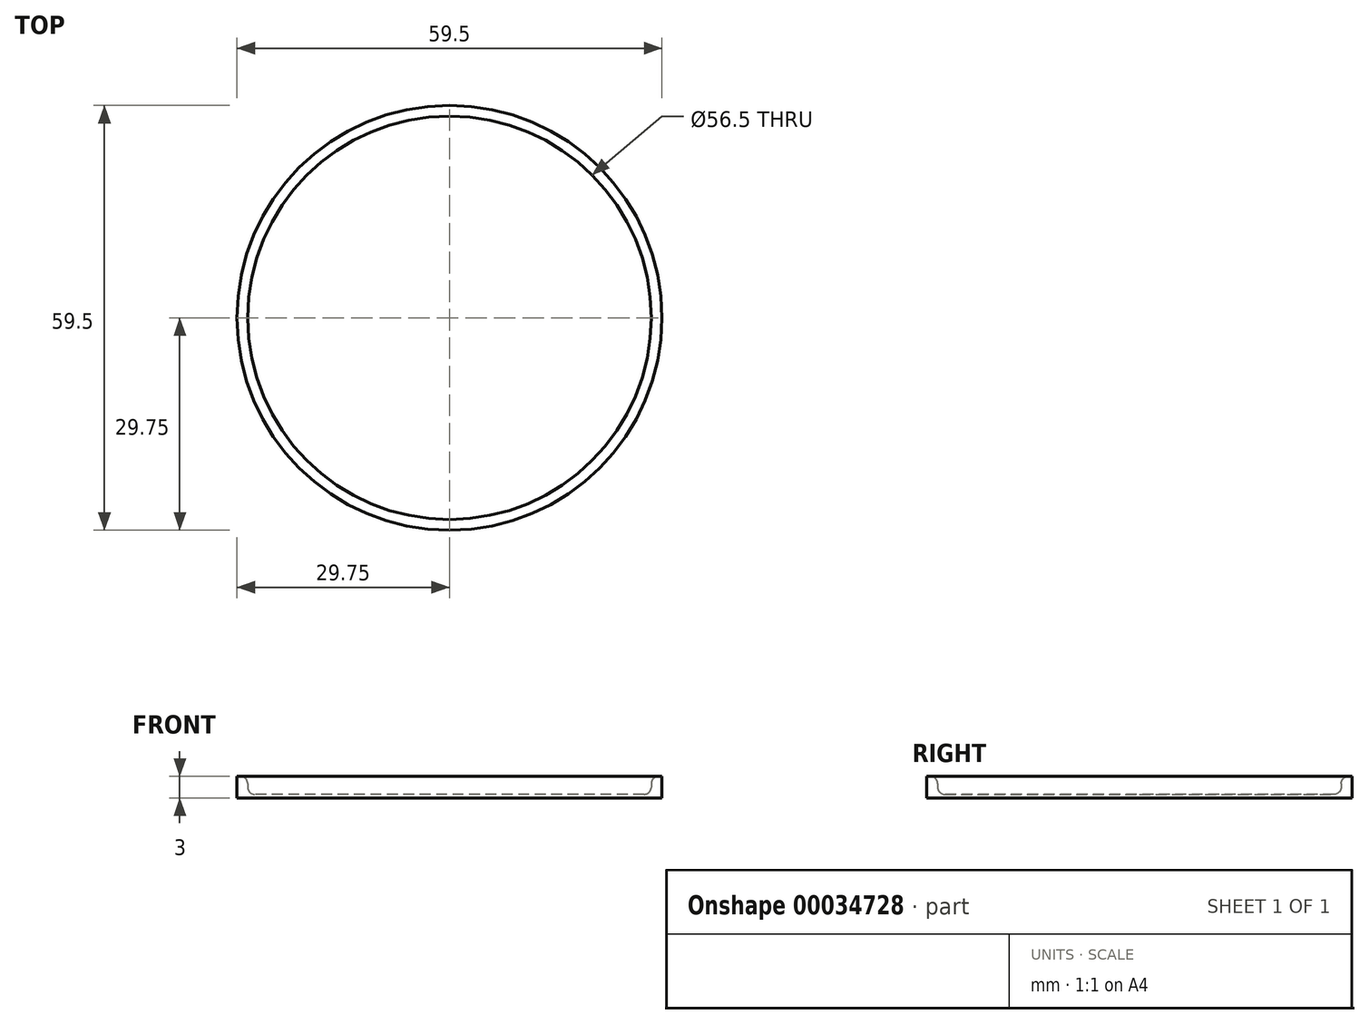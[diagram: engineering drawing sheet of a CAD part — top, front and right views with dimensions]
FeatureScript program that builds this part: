
annotation { "Feature Type Name" : "Feature", "Feature Type Description" : "" }
export const myFeature = defineFeature(function(context is Context, id is Id, definition is map)
    precondition{}
    {
        {
            var Q0;
            Q0=qCreatedBy(makeId("Top.planeOp"),FACE);
            var sketch = newSketch(context, id + "F0", { "sketchPlane" : qUnion([Q0])});
            skCircle(sketch, "E0", {"center": v(0, 0) * mm, "radius": 29.75 * mm});
            skCircle(sketch, "E1", {"center": v(0, 0) * mm, "radius": 28.25 * mm});
            skSolve(sketch);
        }
        {
            var Q0;
            Q0 = qSketchRegion(id + "F0", true);
            extrude(context, id + "F1", {"entities" : qUnion([Q0]), "depth" : 3 * mm, "offsetDistance" : 25 * mm});
        }
        {
            var Q0;
            Q0=makeQuery(id+"F0.imprint","IMPRINT",FACE,{"disambiguationData":[TD([[makeQuery(id+"F0.imprint","IMPRINT",EDGE,{"derivedFrom":sQuery(id+"F0.wireOp",EDGE,"E0")}),1.0]])]});
            var Q1;
            Q1=makeQuery(id+"F0.imprint","IMPRINT",FACE,{"disambiguationData":[TD([[makeQuery(id+"F0.imprint","IMPRINT",EDGE,{"derivedFrom":sQuery(id+"F0.wireOp",EDGE,"E1")}),1.0]])]});
            extrude(context, id + "F2", {"entities" : qUnion([Q0, Q1]), "operationType" : NewBodyOperationType.ADD, "depth" : 0.5 * mm, "offsetDistance" : 25 * mm});
        }
        {
            var Q0;
            Q0=makeQuery(id+"F1.opExtrude","CAP_EDGE",EDGE,{"disambiguationData":[OSD([sQuery(id+"F0.wireOp",EDGE,"E1")])],"isStart":false});
            var Q1;
            Q1=makeQuery(id+"F2.boolean.opBoolean","INTERSECT",EDGE,{"derivedFrom":[makeQuery(id+"F1.opExtrude","SWEPT_FACE",FACE,{"disambiguationData":[OSD([sQuery(id+"F0.wireOp",EDGE,"E1")])]}),makeQuery(id+"F2.opExtrude","CAP_FACE",FACE,{"disambiguationData":[OSD([sQuery(id+"F0.wireOp",EDGE,"E0")])],"isStart":false})]});
            fillet(context, id + "F3", {"entities" : qUnion([Q0, Q1]), "radius" : 1 * mm, "tangentPropagation" : true, "allowEdgeOverflow" : false});
        }
    });
